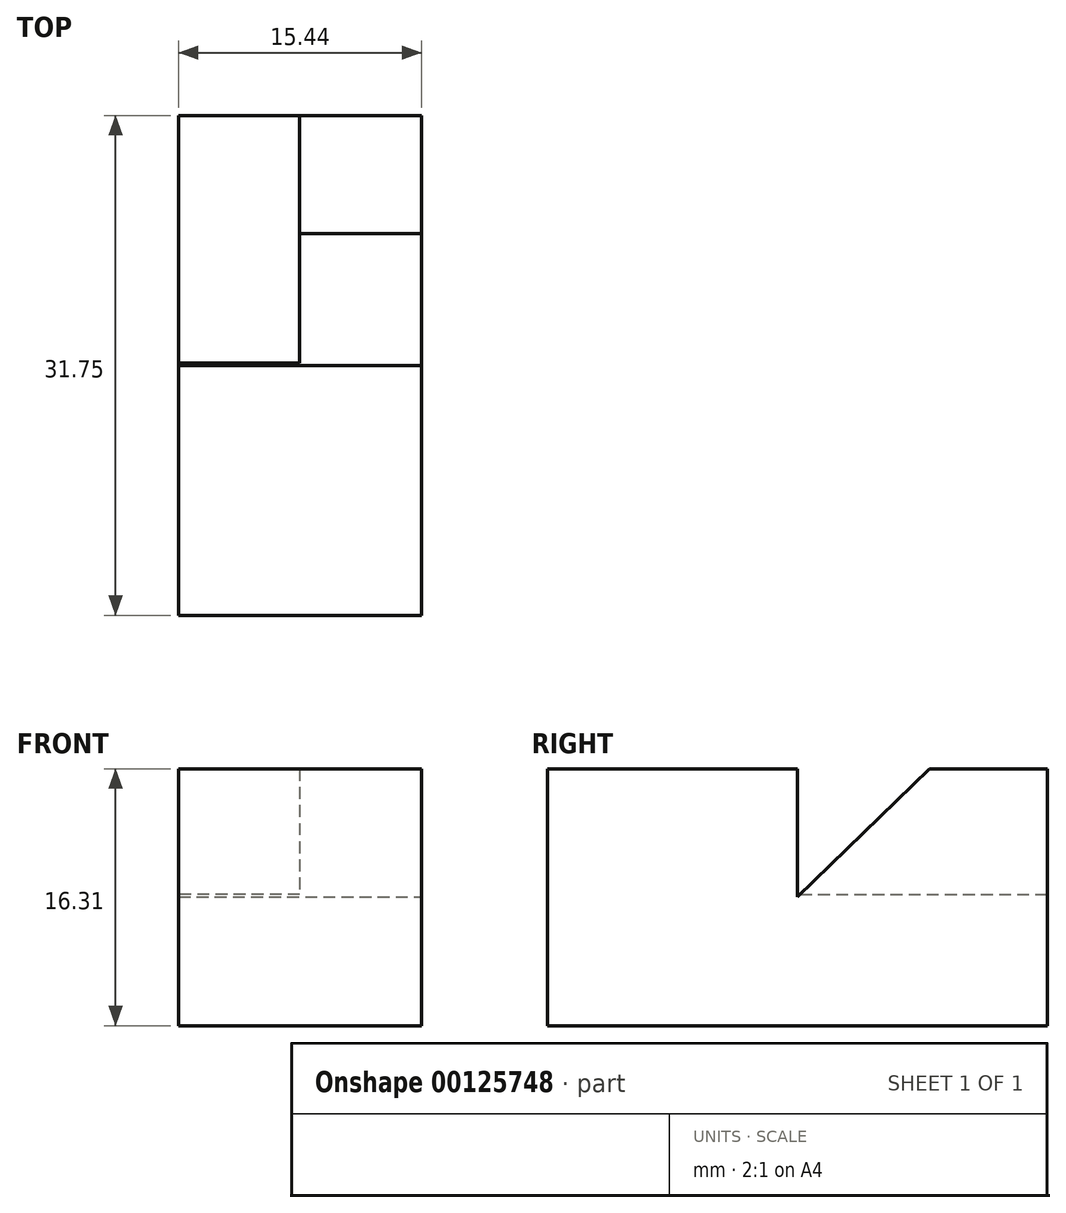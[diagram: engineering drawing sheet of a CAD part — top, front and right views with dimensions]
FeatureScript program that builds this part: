
annotation { "Feature Type Name" : "Feature", "Feature Type Description" : "" }
export const myFeature = defineFeature(function(context is Context, id is Id, definition is map)
    precondition{}
    {
        {
            var Q0;
            Q0=qCreatedBy(makeId("Top.planeOp"),FACE);
            var sketch = newSketch(context, id + "F0", { "sketchPlane" : qUnion([Q0])});
            skLineSegment(sketch, "E0", {"start": v(0, 0) * mm, "end": v(0, 23.93) * mm});
            skLineSegment(sketch, "E1", {"start": v(0, 23.93) * mm, "end": v(-15.44, 23.93) * mm});
            skLineSegment(sketch, "E2", {"start": v(-15.44, 23.93) * mm, "end": v(-15.44, -7.82) * mm});
            skLineSegment(sketch, "E3", {"start": v(-15.44, -7.82) * mm, "end": v(0, -7.82) * mm});
            skLineSegment(sketch, "E4.top", {"start": v(-15.44, 7.8) * mm, "end": v(0, 7.8) * mm});
            skLineSegment(sketch, "E4.left", {"start": v(-15.44, -7.82) * mm, "end": v(-15.44, 7.8) * mm});
            skLineSegment(sketch, "E4.right", {"start": v(0, -7.82) * mm, "end": v(0, 7.8) * mm});
            skSolve(sketch);
        }
        {
            var Q0;
            Q0=qSketchRegion(id+"F0",true);
            extrude(context, id + "F1", {"entities" : qUnion([Q0]), "depth" : 16.3 * mm});
        }
        {
            var Q0;
            Q0=makeQuery(id+"F1.opExtrude","SWEPT_FACE",FACE,{"disambiguationData":[OSD([sQuery(id+"F0.wireOp",EDGE,"E2"),sQuery(id+"F0.wireOp",EDGE,"E4.left")])]});
            var sketch = newSketch(context, id + "F2", { "sketchPlane" : qUnion([Q0])});
            skLineSegment(sketch, "E5", {"start": v(-8.05, 16.3) * mm, "end": v(-8.05, 8.33) * mm});
            skLineSegment(sketch, "E6", {"start": v(-8.05, 8.33) * mm, "end": v(-23.93, 8.33) * mm});
            skSolve(sketch);
        }
        {
            var Q0;
            {var subQ0=sQuery(id+"F2.wireOp",EDGE,"E5");Q0=makeQuery(id+"F2.imprint","IMPRINT",FACE,{"disambiguationData":[TD([[makeQuery(id+"F2.imprint","IMPRINT",EDGE,{"derivedFrom":subQ0}),-1.0]])]});}
            extrude(context, id + "F3", {"entities" : qUnion([Q0]), "operationType" : NewBodyOperationType.REMOVE, "oppositeDirection" : true, "depth" : 7.7 * mm});
        }
        {
            var Q0;
            Q0=makeQuery(id+"FpSYTmIgO3IdqZG_1.boolean.opBoolean","MERGE",FACE,{"derivedFrom":[makeQuery(id+"F1.opExtrude","SWEPT_FACE",FACE,{"disambiguationData":[OSD([sQuery(id+"F0.wireOp",EDGE,"E0"),sQuery(id+"F0.wireOp",EDGE,"E4.right")])]}),makeQuery(id+"FpSYTmIgO3IdqZG_1.opExtrude","SWEPT_FACE",FACE,{"disambiguationData":[OSD([sQuery(id+"FcNOtDJd0nY9frQ_1.wireOp",EDGE,"CNC2rjO0-QE4I-5P5f-L8z3-yzoUwSirhFCQ")])]})]});
            var sketch = newSketch(context, id + "F4", { "sketchPlane" : qUnion([Q0])});
            skLineSegment(sketch, "E7", {"start": v(8.05, 16.3) * mm, "end": v(8.05, 8.18) * mm});
            skLineSegment(sketch, "E8", {"start": v(8.05, 16.3) * mm, "end": v(16.43, 16.3) * mm});
            skLineSegment(sketch, "E9", {"start": v(8.05, 8.18) * mm, "end": v(16.43, 16.3) * mm});
            skSolve(sketch);
        }
        {
            var Q0;
            Q0=makeQuery(id+"F4.imprint","IMPRINT",FACE,{"disambiguationData":[TD([[makeQuery(id+"F4.imprint","IMPRINT",EDGE,{"derivedFrom":sQuery(id+"F4.wireOp",EDGE,"E7")}),1.0]])]});
            extrude(context, id + "F5", {"entities" : qUnion([Q0]), "operationType" : NewBodyOperationType.REMOVE, "oppositeDirection" : true, "depth" : 25.4 * mm});
        }
    });
